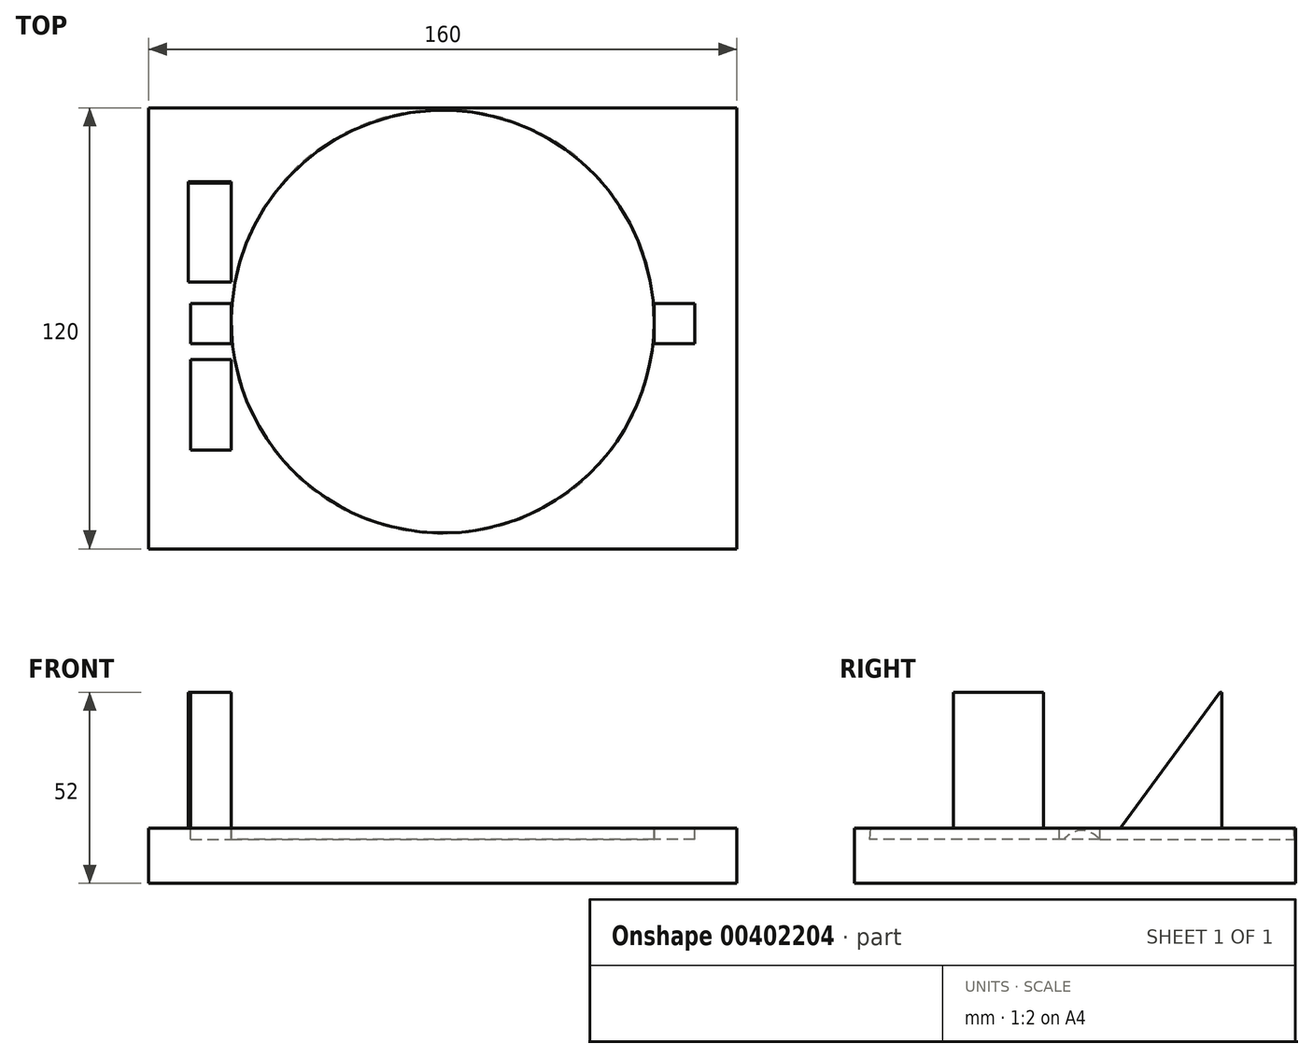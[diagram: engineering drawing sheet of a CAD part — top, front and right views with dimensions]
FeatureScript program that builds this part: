
annotation { "Feature Type Name" : "Feature", "Feature Type Description" : "" }
export const myFeature = defineFeature(function(context is Context, id is Id, definition is map)
    precondition{}
    {
        {
            var Q0;
            Q0=qCreatedBy(makeId("Top.planeOp"),FACE);
            var sketch = newSketch(context, id + "F0", { "sketchPlane" : qUnion([Q0])});
            skLineSegment(sketch, "E0.bottom", {"start": v(-80, 58.15) * mm, "end": v(80, 58.15) * mm});
            skLineSegment(sketch, "E0.top", {"start": v(-80, -61.85) * mm, "end": v(80, -61.85) * mm});
            skLineSegment(sketch, "E0.left", {"start": v(-80, 58.15) * mm, "end": v(-80, -61.85) * mm});
            skLineSegment(sketch, "E0.right", {"start": v(80, 58.15) * mm, "end": v(80, -61.85) * mm});
            skLineSegment(sketch, "E1", {"start": v(-80, -1.85) * mm, "end": v(80, -1.85) * mm});
            skLineSegment(sketch, "E2", {"start": v(0, 58.15) * mm, "end": v(0, -61.85) * mm});
            skSolve(sketch);
        }
        {
            var Q0;
            {var subQ0=sQuery(id+"F0.wireOp",EDGE,"E0.left");var subQ1=sQuery(id+"F0.wireOp",EDGE,"E0.bottom");var subQ2=makeQuery(id+"F0.imprint","INTERSECT",VERTEX,{"derivedFrom":[subQ1,subQ0]});Q0=makeQuery(id+"F0.imprint","IMPRINT",FACE,{"disambiguationData":[TD([[makeQuery(id+"F0.imprint","IMPRINT",EDGE,{"disambiguationData":[TD([[subQ2,-1.0]])],"derivedFrom":subQ1}),-1.0]])]});}
            var Q1;
            {var subQ0=sQuery(id+"F0.wireOp",EDGE,"E0.right");var subQ1=sQuery(id+"F0.wireOp",EDGE,"E0.bottom");var subQ2=makeQuery(id+"F0.imprint","INTERSECT",VERTEX,{"derivedFrom":[subQ1,subQ0]});Q1=makeQuery(id+"F0.imprint","IMPRINT",FACE,{"disambiguationData":[TD([[makeQuery(id+"F0.imprint","IMPRINT",EDGE,{"disambiguationData":[TD([[subQ2,1.0]])],"derivedFrom":subQ1}),-1.0]])]});}
            var Q2;
            {var subQ0=sQuery(id+"F0.wireOp",EDGE,"E0.right");var subQ1=sQuery(id+"F0.wireOp",EDGE,"E0.top");var subQ2=makeQuery(id+"F0.imprint","INTERSECT",VERTEX,{"derivedFrom":[subQ1,subQ0]});Q2=makeQuery(id+"F0.imprint","IMPRINT",FACE,{"disambiguationData":[TD([[makeQuery(id+"F0.imprint","IMPRINT",EDGE,{"disambiguationData":[TD([[subQ2,1.0]])],"derivedFrom":subQ1}),1.0]])]});}
            var Q3;
            {var subQ0=sQuery(id+"F0.wireOp",EDGE,"E0.left");var subQ1=sQuery(id+"F0.wireOp",EDGE,"E0.top");var subQ2=makeQuery(id+"F0.imprint","INTERSECT",VERTEX,{"derivedFrom":[subQ1,subQ0]});Q3=makeQuery(id+"F0.imprint","IMPRINT",FACE,{"disambiguationData":[TD([[makeQuery(id+"F0.imprint","IMPRINT",EDGE,{"disambiguationData":[TD([[subQ2,-1.0]])],"derivedFrom":subQ1}),1.0]])]});}
            extrude(context, id + "F1", {"entities" : qUnion([Q0, Q1, Q2, Q3]), "oppositeDirection" : true, "depth" : 15 * mm});
        }
        {
            var Q0;
            Q0=qCreatedBy(makeId("Top.planeOp"),FACE);
            var sketch = newSketch(context, id + "F2", { "sketchPlane" : qUnion([Q0])});
            skCircle(sketch, "E3", {"center": v(0, 0) * mm, "radius": 57.5 * mm});
            skSolve(sketch);
        }
        {
            var Q0;
            Q0 = qSketchRegion(id + "F2", true);
            extrude(context, id + "F3", {"entities" : qUnion([Q0]), "operationType" : NewBodyOperationType.REMOVE, "oppositeDirection" : true, "depth" : 3 * mm, "hasDraft" : true, "draftAngle" : 5 * degree});
        }
        {
            var Q0;
            Q0=qCreatedBy(makeId("Top.planeOp"),FACE);
            var sketch = newSketch(context, id + "F4", { "sketchPlane" : qUnion([Q0])});
            skLineSegment(sketch, "E4.bottom", {"start": v(-68.55, 4.94) * mm, "end": v(-57.55, 4.94) * mm});
            skLineSegment(sketch, "E4.top", {"start": v(-68.55, -6.06) * mm, "end": v(-57.55, -6.06) * mm});
            skLineSegment(sketch, "E4.left", {"start": v(-68.55, 4.94) * mm, "end": v(-68.55, -6.06) * mm});
            skLineSegment(sketch, "E4.right", {"start": v(-57.55, 4.94) * mm, "end": v(-57.55, -6.06) * mm});
            skLineSegment(sketch, "E5.MirrorCS", {"start": v(68.55, 4.94) * mm, "end": v(57.55, 4.94) * mm});
            skLineSegment(sketch, "E6.MirrorCS", {"start": v(68.55, 4.94) * mm, "end": v(68.55, -6.06) * mm});
            skLineSegment(sketch, "E7.MirrorCS", {"start": v(68.55, -6.06) * mm, "end": v(57.55, -6.06) * mm});
            skLineSegment(sketch, "E8.MirrorCS", {"start": v(57.55, 4.94) * mm, "end": v(57.55, -6.06) * mm});
            skLineSegment(sketch, "E9.bottom", {"start": v(-69.2, 38.06) * mm, "end": v(-57.55, 38.06) * mm});
            skLineSegment(sketch, "E9.top", {"start": v(-69.2, 10.7) * mm, "end": v(-57.55, 10.7) * mm});
            skLineSegment(sketch, "E9.left", {"start": v(-69.2, 38.06) * mm, "end": v(-69.2, 10.7) * mm});
            skLineSegment(sketch, "E9.right", {"start": v(-57.55, 38.06) * mm, "end": v(-57.55, 10.7) * mm});
            skLineSegment(sketch, "E10.bottom", {"start": v(-68.55, -10.35) * mm, "end": v(-57.55, -10.35) * mm});
            skLineSegment(sketch, "E10.top", {"start": v(-68.55, -34.9) * mm, "end": v(-57.55, -34.9) * mm});
            skLineSegment(sketch, "E10.left", {"start": v(-68.55, -10.35) * mm, "end": v(-68.55, -34.9) * mm});
            skLineSegment(sketch, "E10.right", {"start": v(-57.55, -10.35) * mm, "end": v(-57.55, -34.9) * mm});
            skSolve(sketch);
        }
        {
            var Q0;
            Q0=makeQuery(id+"F4.imprint","IMPRINT",FACE,{"disambiguationData":[TD([[makeQuery(id+"F4.imprint","IMPRINT",EDGE,{"derivedFrom":sQuery(id+"F4.wireOp",EDGE,"E9.bottom")}),-1.0]])]});
            var Q1;
            Q1=makeQuery(id+"F4.imprint","IMPRINT",FACE,{"disambiguationData":[TD([[makeQuery(id+"F4.imprint","IMPRINT",EDGE,{"derivedFrom":sQuery(id+"F4.wireOp",EDGE,"E4.bottom")}),-1.0]])]});
            var Q2;
            Q2=makeQuery(id+"F4.imprint","IMPRINT",FACE,{"disambiguationData":[TD([[makeQuery(id+"F4.imprint","IMPRINT",EDGE,{"derivedFrom":sQuery(id+"F4.wireOp",EDGE,"E10.bottom")}),-1.0]])]});
            var Q3;
            Q3=makeQuery(id+"F4.imprint","IMPRINT",FACE,{"disambiguationData":[TD([[makeQuery(id+"F4.imprint","IMPRINT",EDGE,{"derivedFrom":sQuery(id+"F4.wireOp",EDGE,"E5.MirrorCS")}),1.0]])]});
            extrude(context, id + "F5", {"entities" : qUnion([Q0, Q1, Q2, Q3]), "operationType" : NewBodyOperationType.REMOVE, "oppositeDirection" : true, "depth" : 3 * mm});
        }
        {
            var Q0;
            Q0=makeQuery(id+"F5.boolean.opBoolean","COPY",FACE,{"derivedFrom":makeQuery(id+"F5.opExtrude","CAP_FACE",FACE,{"disambiguationData":[OSD([sQuery(id+"F4.wireOp",EDGE,"E9.bottom"),sQuery(id+"F4.wireOp",EDGE,"E9.top"),sQuery(id+"F4.wireOp",EDGE,"E9.left"),sQuery(id+"F4.wireOp",EDGE,"E9.right")])],"isStart":false})});
            var Q1;
            Q1=makeQuery(id+"F5.boolean.opBoolean","COPY",FACE,{"derivedFrom":makeQuery(id+"F5.opExtrude","CAP_FACE",FACE,{"disambiguationData":[OSD([sQuery(id+"F4.wireOp",EDGE,"E10.bottom"),sQuery(id+"F4.wireOp",EDGE,"E10.top"),sQuery(id+"F4.wireOp",EDGE,"E10.left"),sQuery(id+"F4.wireOp",EDGE,"E10.right")])],"isStart":false})});
            extrude(context, id + "F6", {"entities" : qUnion([Q0, Q1]), "operationType" : NewBodyOperationType.ADD, "depth" : 40 * mm});
        }
        {
            var Q0;
            Q0=makeQuery(id+"F6.opExtrude","SWEPT_FACE",FACE,{"disambiguationData":[OSD([sQuery(id+"F4.wireOp",EDGE,"E9.right")])]});
            cPlane(context, id + "F7", {"entities" : qUnion([Q0]), "cplaneType" : CPlaneType.OFFSET, "offset" : 0 * mm, "width" : 150 * mm, "height" : 150 * mm});
        }
        {
            var Q0;
            Q0=qCreatedBy(id+"F7.planeOp",FACE);
            var sketch = newSketch(context, id + "F8", { "sketchPlane" : qUnion([Q0])});
            skLineSegment(sketch, "E11", {"start": v(10.52, 37.36) * mm, "end": v(10.52, 0) * mm});
            skLineSegment(sketch, "E12", {"start": v(10.52, 0) * mm, "end": v(37.88, 37.36) * mm});
            skLineSegment(sketch, "E13", {"start": v(37.88, 37.36) * mm, "end": v(10.52, 37.36) * mm});
            skSolve(sketch);
        }
        {
            var Q0;
            Q0=makeQuery(id+"F8.imprint","IMPRINT",FACE,{"disambiguationData":[TD([[makeQuery(id+"F8.imprint","IMPRINT",EDGE,{"derivedFrom":sQuery(id+"F8.wireOp",EDGE,"E11")}),1.0]])]});
            extrude(context, id + "F9", {"entities" : qUnion([Q0]), "operationType" : NewBodyOperationType.REMOVE, "endBound" : BoundingType.UP_TO_NEXT, "oppositeDirection" : true, "depth" : 25 * mm});
        }
    });
